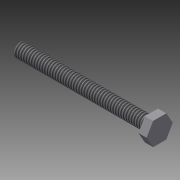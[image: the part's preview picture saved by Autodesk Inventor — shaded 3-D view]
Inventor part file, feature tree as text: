
AUTODESK INVENTOR PART (.ipt)
format: ipt  version: 2015 (Build 190159000, 159)  size: 85,504 bytes
history: native  units: in
note: dims shown in document units (in); Inventor stores cm internally (conversion verified against a paired STEP export)
features: extrude x2, sketch x2, thread x1
ambient origin geometry x8: Origin, YZ Plane, XZ Plane, XY Plane, X Axis, Y Axis, Z Axis, Center Point
bodies: Solid1 (feature_tree)
feature tree (5):
  extrude  "Extrusion1"  Depth=2.5in TaperAngle=0.0deg
  thread  "Thread1"  [1 undecoded]
  extrude  "Extrusion2"  Depth=0.1562in TaperAngle=0.0deg
  sketch  "Sketch1"  dims[d0=0.25in d1=2.5in d2=0.0in d3=1.0in d4=0.0in]
  sketch  "Sketch2"  dims[d5=0.5in d6=0.1562in d7=0.0in]
note: 1 required parameter value undecoded (feature->parameter linkage not recoverable at this tier; creation-order binding heuristic only, values carry confidence <= 0.55)
